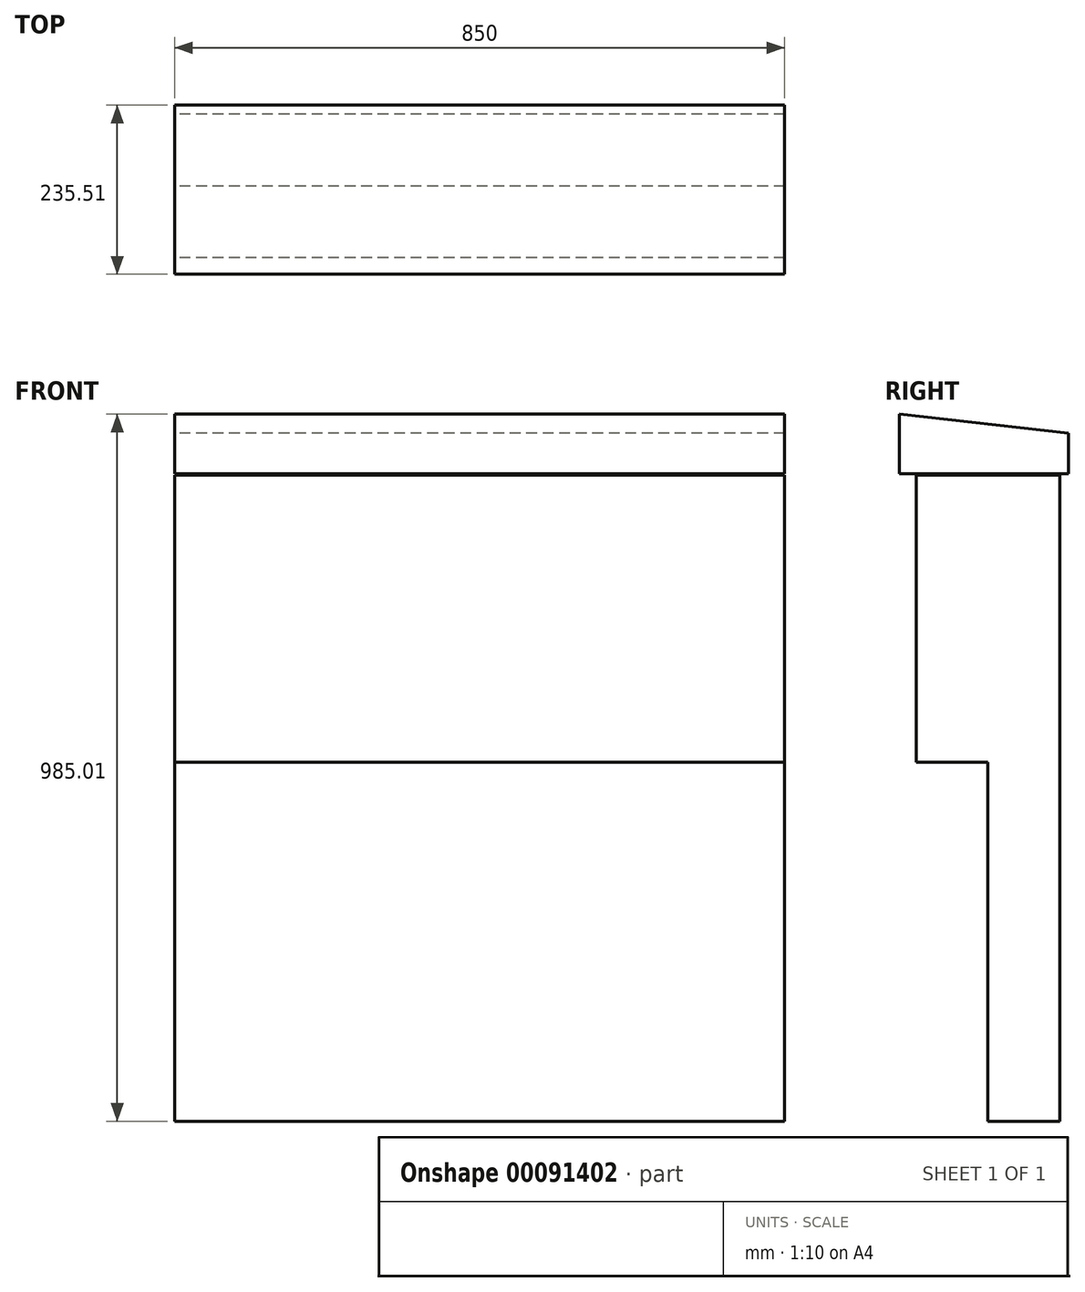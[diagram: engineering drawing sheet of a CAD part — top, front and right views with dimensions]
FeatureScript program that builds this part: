
annotation { "Feature Type Name" : "Feature", "Feature Type Description" : "" }
export const myFeature = defineFeature(function(context is Context, id is Id, definition is map)
    precondition{}
    {
        {
            var Q0;
            Q0=qCreatedBy(makeId("Right.planeOp"),FACE);
            var sketch = newSketch(context, id + "F0", { "sketchPlane" : qUnion([Q0])});
            skLineSegment(sketch, "E0.top", {"start": v(-100, -294.93) * mm, "end": v(0, -294.93) * mm});
            skLineSegment(sketch, "E0.left", {"start": v(-100, 105.07) * mm, "end": v(-100, -294.93) * mm});
            skLineSegment(sketch, "E0.right", {"start": v(100, 105.07) * mm, "end": v(100, -294.93) * mm});
            skLineSegment(sketch, "E1.left", {"start": v(100, -294.93) * mm, "end": v(100, -794.93) * mm});
            skLineSegment(sketch, "E1.right", {"start": v(0, -294.93) * mm, "end": v(0, -794.93) * mm});
            skLineSegment(sketch, "E2", {"start": v(-100, 105.07) * mm, "end": v(100, 105.07) * mm});
            skLineSegment(sketch, "E3", {"start": v(0, -794.93) * mm, "end": v(100, -794.93) * mm});
            skSolve(sketch);
        }
        {
            var Q0;
            Q0=qCreatedBy(makeId("Right.planeOp"),FACE);
            var sketch = newSketch(context, id + "F1", { "sketchPlane" : qUnion([Q0])});
            skLineSegment(sketch, "E4.bottom", {"start": v(-123.03, 107.28) * mm, "end": v(112.48, 107.28) * mm});
            skLineSegment(sketch, "E4.left", {"start": v(-123.03, 107.28) * mm, "end": v(-123.03, 190.08) * mm});
            skLineSegment(sketch, "E4.right", {"start": v(112.48, 107.28) * mm, "end": v(112.48, 163.95) * mm});
            skLineSegment(sketch, "E5", {"start": v(-123.03, 190.08) * mm, "end": v(112.48, 163.95) * mm});
            skSolve(sketch);
        }
        {
            var Q0;
            Q0=qSketchRegion(id+"F0",true);
            extrude(context, id + "F2", {"entities" : qUnion([Q0]), "depth" : 850 * mm});
        }
        {
            var Q0;
            Q0=qSketchRegion(id+"F1",true);
            extrude(context, id + "F3", {"entities" : qUnion([Q0]), "depth" : 850 * mm});
        }
    });
